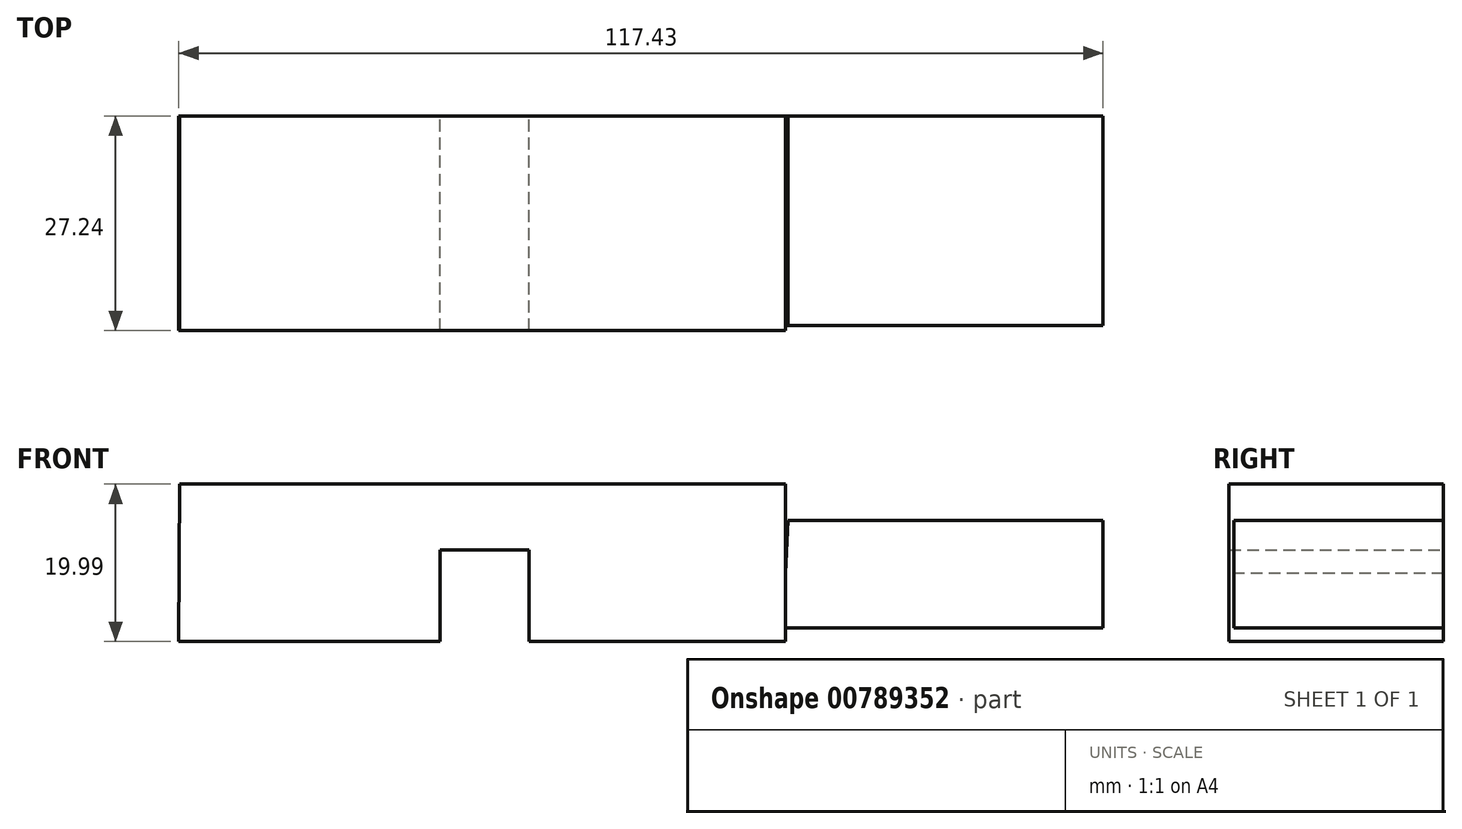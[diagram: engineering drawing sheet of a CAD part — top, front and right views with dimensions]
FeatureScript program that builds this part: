
annotation { "Feature Type Name" : "Feature", "Feature Type Description" : "" }
export const myFeature = defineFeature(function(context is Context, id is Id, definition is map)
    precondition{}
    {
        {
            var Q0;
            Q0=qCreatedBy(makeId("Front.planeOp"),FACE);
            var sketch = newSketch(context, id + "F0", { "sketchPlane" : qUnion([Q0])});
            skLineSegment(sketch, "E0", {"start": v(-63.32, 27.36) * mm, "end": v(63.11, 27.36) * mm});
            skLineSegment(sketch, "E1", {"start": v(63.11, 7.37) * mm, "end": v(-63.47, 7.37) * mm});
            skLineSegment(sketch, "E2", {"start": v(-63.47, 7.37) * mm, "end": v(-63.32, 27.36) * mm});
            skLineSegment(sketch, "E3", {"start": v(63.11, 7.37) * mm, "end": v(63.11, 27.36) * mm});
            skLineSegment(sketch, "E4", {"start": v(35.8, 7.37) * mm, "end": v(35.8, 27.36) * mm});
            skLineSegment(sketch, "E5", {"start": v(35.8, 27.36) * mm, "end": v(13.6, 27.36) * mm});
            skLineSegment(sketch, "E6", {"start": v(13.6, 27.36) * mm, "end": v(13.6, 7.37) * mm});
            skLineSegment(sketch, "E7", {"start": v(13.6, 7.37) * mm, "end": v(35.8, 7.37) * mm});
            skLineSegment(sketch, "E8", {"start": v(-30.29, 7.37) * mm, "end": v(-30.29, 18.97) * mm});
            skLineSegment(sketch, "E9", {"start": v(-30.29, 18.97) * mm, "end": v(-18.93, 18.97) * mm});
            skLineSegment(sketch, "E10", {"start": v(-18.93, 18.97) * mm, "end": v(-18.93, 7.37) * mm});
            skSolve(sketch);
        }
        {
            var Q0;
            {var subQ3=sQuery(id+"F0.wireOp",EDGE,"E2");Q0=makeQuery(id+"F0.imprint","IMPRINT",FACE,{"disambiguationData":[TD([[makeQuery(id+"F0.imprint","IMPRINT",EDGE,{"derivedFrom":subQ3}),-1.0]])]});}
            extrude(context, id + "F1", {"entities" : qUnion([Q0]), "depth" : 27.24 * mm, "offsetDistance" : 25.4 * mm});
        }
        {
            var Q0;
            Q0=qCreatedBy(makeId("Front.planeOp"),FACE);
            var sketch = newSketch(context, id + "F2", { "sketchPlane" : qUnion([Q0])});
            skLineSegment(sketch, "E11", {"start": v(13.9, 22.77) * mm, "end": v(53.96, 22.77) * mm});
            skLineSegment(sketch, "E12", {"start": v(53.96, 22.77) * mm, "end": v(53.96, 9.08) * mm});
            skLineSegment(sketch, "E13", {"start": v(53.96, 9.08) * mm, "end": v(13.28, 9.08) * mm});
            skLineSegment(sketch, "E14", {"start": v(13.28, 9.08) * mm, "end": v(13.9, 22.77) * mm});
            skSolve(sketch);
        }
        {
            var Q0;
            Q0=makeQuery(id+"F2.imprint","IMPRINT",FACE,{"disambiguationData":[TD([[makeQuery(id+"F2.imprint","IMPRINT",EDGE,{"derivedFrom":sQuery(id+"F2.wireOp",EDGE,"E11")}),-1.0]])]});
            var Q1;
            Q1 = qSketchRegion(id + "F2", true);
            extrude(context, id + "F3", {"entities" : qUnion([Q0, Q1]), "operationType" : NewBodyOperationType.ADD, "depth" : 26.62 * mm, "offsetDistance" : 25.4 * mm});
        }
    });
